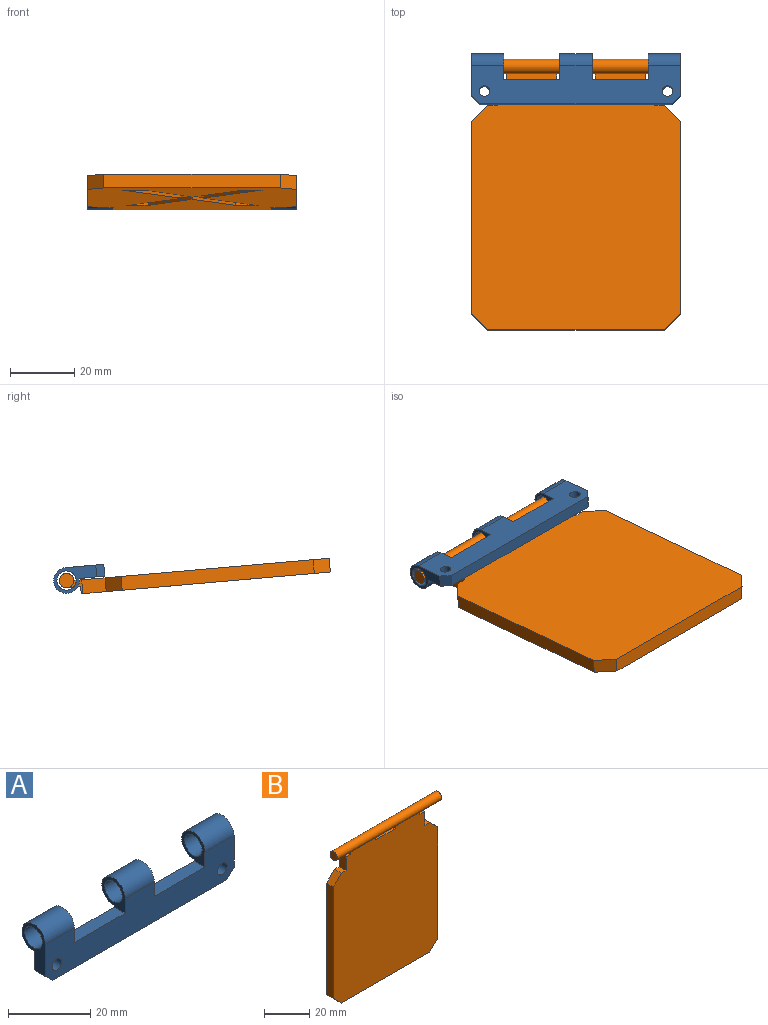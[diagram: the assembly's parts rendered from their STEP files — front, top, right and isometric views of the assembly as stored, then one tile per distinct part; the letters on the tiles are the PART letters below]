
ASSEMBLY  parts=2 mates=1
PART A: 21 faces, bbox 65x8x16 mm
  f0: plane 60x3.7mm, normal (0,0,-1), area 222mm2, adj f2,f3,f12,f20
  f1: plane 13.5x8mm, normal (1,0,0), area 45.8mm2, adj f2,f3,f4,f5,f12
  f2: plane 65x12mm, normal (0,-1,0), area 599.5mm2, adj f0,f1,f5,f7,f8,f9,f10,f11
  f3: plane 65x8.01mm, normal (0,1,0), area 479.9mm2, adj f0,f1,f5,f7,f8,f9,f10,f11
  f4: cylinder r=3mm len=10mm, axis (-1,0,0), area 188.5mm2, adj f1,f9
  f5: cylinder r=4mm len=10mm, axis (-1,0,0), area 191.5mm2, adj f1,f2,f3,f9
  f6: cylinder r=3mm len=10mm, axis (-1,0,0), area 188.5mm2, adj f10,f18
  f7: cylinder r=4mm len=10mm, axis (-1,0,0), area 191.5mm2, adj f2,f3,f10,f18
  f8: plane 17.5x3.7mm, normal (0,0,1), area 64.7mm2, adj f2,f3,f9,f10
  f9: plane 8.49x8mm, normal (-1,0,0), area 27.2mm2, adj f2,f3,f4,f5,f8
  f10: plane 8.49x8mm, normal (1,0,0), area 27.2mm2, adj f2,f3,f6,f7,f8
  f11: cylinder r=1.65mm len=3.7mm, axis (0,1,0), area 38.4mm2, adj f2,f3
  f12: plane 3.7x2.5mm, normal (0.71,0,-0.71), area 13.1mm2, adj f0,f1,f2,f3
  f13: plane 13.5x8mm, normal (-1,0,0), area 45.8mm2, adj f2,f3,f14,f15,f20
  f14: cylinder r=3mm len=10mm, axis (1,0,0), area 188.5mm2, adj f13,f17
  f15: cylinder r=4mm len=10mm, axis (1,0,0), area 191.5mm2, adj f2,f3,f13,f17
  f16: plane 17.5x3.7mm, normal (0,0,1), area 64.7mm2, adj f2,f3,f17,f18
  f17: plane 8.49x8mm, normal (1,0,0), area 27.2mm2, adj f2,f3,f14,f15,f16
  f18: plane 8.49x8mm, normal (-1,0,0), area 27.2mm2, adj f2,f3,f6,f7,f16
  f19: cylinder r=1.65mm len=3.7mm, axis (0,1,0), area 38.4mm2, adj f2,f3
  f20: plane 3.7x2.5mm, normal (-0.71,0,-0.71), area 13.1mm2, adj f0,f2,f3,f13
PART B: 40 faces, bbox 65x6.8x84.3 mm
  f0: plane 77.8x65mm, normal (0,1,0), area 4173.2mm2, adj f1,f2,f5,f7,f8,f10,f11,f12
  f1: plane 4.7x4.3mm, normal (-1,0,0), area 7.2mm2, adj f0,f3,f4,f5,f6,f7
  f2: plane 4.7x4.3mm, normal (1,0,0), area 7.2mm2, adj f0,f3,f4,f5,f6,f8
  f3: plane 15.5x4.2mm, normal (0,1,0), area 65.1mm2, adj f1,f2,f4,f5
  f4: cylinder r=2.25mm len=65mm, axis (-1,0,0), area 815.6mm2, adj f1,f2,f3,f6,f9,f16,f17,f18
  f5: plane 15.5x2.25mm, normal (0,0,1), area 34.9mm2, adj f0,f1,f2,f3
  f6: plane 79.76x65mm, normal (0,-1,0), area 4933.9mm2, adj f1,f2,f4,f7,f8,f10,f11,f12
  f7: plane 12x4.3mm, normal (0,0,1), area 51.6mm2, adj f0,f1,f6,f16
  f8: plane 4.3x3mm, normal (0,0,1), area 12.9mm2, adj f0,f2,f6,f10
  f9: plane 4.5x4.5mm, normal (1,0,0), area 15.9mm2, adj f4
  f10: plane 7.3x4.3mm, normal (1,0,0), area 31.4mm2, adj f0,f6,f8,f11
  f11: plane 4.3x3mm, normal (0,0,1), area 12.9mm2, adj f0,f6,f10,f15
  f12: plane 60x4.3mm, normal (1,0,0), area 258mm2, adj f0,f6,f14,f15
  f13: plane 55x4.3mm, normal (0,0,-1), area 236.5mm2, adj f0,f6,f14,f25
  f14: plane 5x5mm, normal (0.71,0,-0.71), area 30.4mm2, adj f0,f6,f12,f13
  f15: plane 5x5mm, normal (0.71,0,0.71), area 30.4mm2, adj f0,f6,f11,f12
  f16: plane 4.7x4.3mm, normal (1,0,0), area 7.2mm2, adj f0,f4,f6,f7,f18,f19
  f17: plane 4.7x4.3mm, normal (-1,0,0), area 7.2mm2, adj f0,f4,f6,f18,f19,f20
  f18: plane 15.5x4.2mm, normal (0,1,0), area 65.1mm2, adj f4,f16,f17,f19
  f19: plane 15.5x2.25mm, normal (0,0,1), area 34.9mm2, adj f0,f16,f17,f18
  f20: plane 4.3x3mm, normal (0,0,1), area 12.9mm2, adj f0,f6,f17,f22
  f21: plane 4.5x4.5mm, normal (-1,0,0), area 15.9mm2, adj f4
  f22: plane 7.3x4.3mm, normal (-1,0,0), area 31.4mm2, adj f0,f6,f20,f23
  f23: plane 4.3x3mm, normal (0,0,1), area 12.9mm2, adj f0,f6,f22,f26
  f24: plane 60x4.3mm, normal (-1,0,0), area 258mm2, adj f0,f6,f25,f26
  f25: plane 5x5mm, normal (-0.71,0,-0.71), area 30.4mm2, adj f0,f6,f13,f24
  f26: plane 5x5mm, normal (-0.71,0,0.71), area 30.4mm2, adj f0,f6,f23,f24
  f27: plane 7.2x1mm, normal (0,0,1), area 7.2mm2, adj f0,f28,f38,f39
  f28: plane 28.72x18.2mm, normal (0.84,0,-0.54), area 34mm2, adj f0,f27,f29,f39
  f29: plane 25.82x16.89mm, normal (0.84,0,0.55), area 30.9mm2, adj f0,f28,f30,f39
  f30: plane 6.74x1mm, normal (0,0,-1), area 6.7mm2, adj f0,f29,f31,f39
  f31: plane 21.6x13.65mm, normal (-0.85,0,-0.53), area 25.6mm2, adj f0,f30,f32,f39
  f32: plane 21.6x13.54mm, normal (0.85,0,-0.53), area 25.5mm2, adj f0,f31,f33,f39
  f33: plane 7.02x1mm, normal (0,0,-1), area 7mm2, adj f0,f32,f34,f39
  f34: plane 26.03x16.9mm, normal (-0.84,0,0.54), area 31mm2, adj f0,f33,f35,f39
  f35: plane 28.5x18.13mm, normal (-0.84,0,-0.54), area 33.8mm2, adj f0,f34,f36,f39
  f36: plane 6.72x1mm, normal (0,0,1), area 6.7mm2, adj f0,f35,f37,f39
  f37: plane 23.98x14.92mm, normal (0.85,0,0.53), area 28.2mm2, adj f0,f36,f38,f39
  f38: plane 23.98x14.66mm, normal (-0.85,0,0.52), area 28.1mm2, adj f0,f27,f37,f39
  f39: plane 54.53x43.49mm, normal (0,1,0), area 700mm2, adj f27,f28,f29,f30,f31,f32,f33,f34
PLACE A rot(axis=(-1,0,0),95.2deg) t=(1.52,25.96,-16.19)mm
PLACE B rot(axis=(-1,0,0),95deg) t=(1.52,25.72,1.95)mm
MATE revolute A.f4 <-> B.f4  axis (1,0,0) through (34.02,25.96,-16.19)mm
